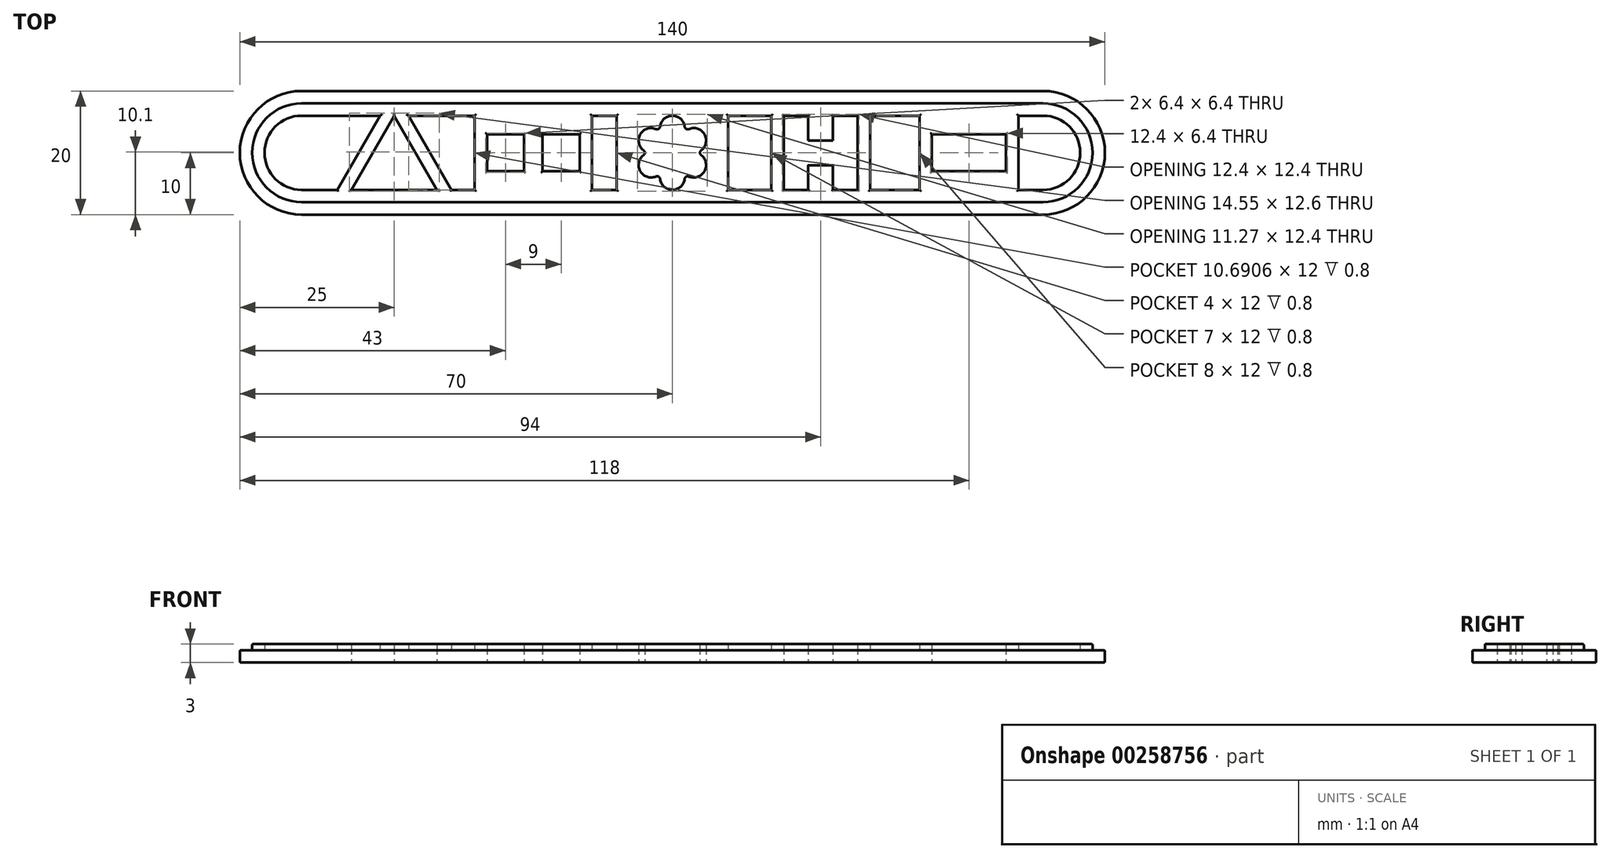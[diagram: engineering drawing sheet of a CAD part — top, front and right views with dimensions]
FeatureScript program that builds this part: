
annotation { "Feature Type Name" : "Feature", "Feature Type Description" : "" }
export const myFeature = defineFeature(function(context is Context, id is Id, definition is map)
    precondition{}
    {
        {
            var Q0;
            Q0=qCreatedBy(makeId("Top.planeOp"),FACE);
            var sketch = newSketch(context, id + "F0", { "sketchPlane" : qUnion([Q0])});
            skLineSegment(sketch, "E0.bottom", {"start": v(-60, -10) * mm, "end": v(60, -10) * mm});
            skLineSegment(sketch, "E0.top", {"start": v(-60, 10) * mm, "end": v(60, 10) * mm});
            skPoint(sketch, "E0.middle", {"position": v(0, 0) * mm});
            skArc(sketch, "E1", {"start": v(-60, 10) * mm, "mid": v(-70, 0) * mm, "end": v(-60, -10) * mm});
            skArc(sketch, "E2", {"start": v(60, -10) * mm, "mid": v(70, 0) * mm, "end": v(60, 10) * mm});
            skLineSegment(sketch, "E3", {"start": v(-70, 0) * mm, "end": v(70, 0) * mm, "construction": true});
            skArc(sketch, "E4", {"start": v(1.99, 4.24) * mm, "mid": v(0, 6) * mm, "end": v(-1.99, 4.24) * mm});
            skArc(sketch, "E5.1.0", {"start": v(-2.68, 3.84) * mm, "mid": v(-5.2, 3) * mm, "end": v(-4.66, 0.4) * mm});
            skArc(sketch, "E5.2.0", {"start": v(-4.66, -0.4) * mm, "mid": v(-5.2, -3) * mm, "end": v(-2.68, -3.84) * mm});
            skArc(sketch, "E5.3.0", {"start": v(-1.99, -4.24) * mm, "mid": v(0, -6) * mm, "end": v(1.99, -4.24) * mm});
            skArc(sketch, "E5.4.0", {"start": v(2.68, -3.84) * mm, "mid": v(5.2, -3) * mm, "end": v(4.66, -0.4) * mm});
            skArc(sketch, "E5.5.0", {"start": v(4.66, 0.4) * mm, "mid": v(5.2, 3) * mm, "end": v(2.68, 3.84) * mm});
            skPoint(sketch, "E6.visualSharp", {"position": v(-1.73, 3) * mm});
            skArc(sketch, "E6.filletArc", {"start": v(-2.68, 3.84) * mm, "mid": v(-2.23, 3.87) * mm, "end": v(-1.99, 4.24) * mm});
            skPoint(sketch, "E7.visualSharp", {"position": v(1.73, 3) * mm});
            skArc(sketch, "E7.filletArc", {"start": v(1.99, 4.24) * mm, "mid": v(2.23, 3.87) * mm, "end": v(2.68, 3.84) * mm});
            skPoint(sketch, "E8.visualSharp", {"position": v(3.46, 0) * mm});
            skArc(sketch, "E8.filletArc", {"start": v(4.66, 0.4) * mm, "mid": v(4.46, 0) * mm, "end": v(4.66, -0.4) * mm});
            skPoint(sketch, "E9.visualSharp", {"position": v(1.73, -3) * mm});
            skArc(sketch, "E9.filletArc", {"start": v(2.68, -3.84) * mm, "mid": v(2.23, -3.87) * mm, "end": v(1.99, -4.24) * mm});
            skPoint(sketch, "E10.visualSharp", {"position": v(-1.73, -3) * mm});
            skArc(sketch, "E10.filletArc", {"start": v(-1.99, -4.24) * mm, "mid": v(-2.23, -3.87) * mm, "end": v(-2.68, -3.84) * mm});
            skPoint(sketch, "E11.visualSharp", {"position": v(-3.46, 0) * mm});
            skArc(sketch, "E11.filletArc", {"start": v(-4.66, -0.4) * mm, "mid": v(-4.46, 0) * mm, "end": v(-4.66, 0.4) * mm});
            skLineSegment(sketch, "E12.bottom", {"start": v(-15, 3) * mm, "end": v(-21, 3) * mm});
            skLineSegment(sketch, "E12.top", {"start": v(-15, -3) * mm, "end": v(-21, -3) * mm});
            skLineSegment(sketch, "E12.left", {"start": v(-15, 3) * mm, "end": v(-15, -3) * mm});
            skLineSegment(sketch, "E12.right", {"start": v(-21, 3) * mm, "end": v(-21, -3) * mm});
            skPoint(sketch, "E12.middle", {"position": v(-18, 0) * mm});
            skLineSegment(sketch, "E13.bottom", {"start": v(-24, -3) * mm, "end": v(-30, -3) * mm});
            skLineSegment(sketch, "E13.top", {"start": v(-24, 3) * mm, "end": v(-30, 3) * mm});
            skLineSegment(sketch, "E13.left", {"start": v(-24, -3) * mm, "end": v(-24, 3) * mm});
            skLineSegment(sketch, "E13.right", {"start": v(-30, -3) * mm, "end": v(-30, 3) * mm});
            skPoint(sketch, "E13.middle", {"position": v(-27, 0) * mm});
            skLineSegment(sketch, "E14", {"start": v(-51.93, -6) * mm, "end": v(-38.07, -6) * mm});
            skLineSegment(sketch, "E15", {"start": v(-38.07, -6) * mm, "end": v(-45, 6) * mm});
            skLineSegment(sketch, "E16", {"start": v(-45, 6) * mm, "end": v(-51.93, -6) * mm});
            skLineSegment(sketch, "E17", {"start": v(-45, 6) * mm, "end": v(-45, -6) * mm, "construction": true});
            skPoint(sketch, "E18", {"position": v(-45, 0) * mm});
            skLineSegment(sketch, "E19", {"start": v(18, 6) * mm, "end": v(18, -6) * mm});
            skLineSegment(sketch, "E20", {"start": v(18, -6) * mm, "end": v(22, -6) * mm});
            skLineSegment(sketch, "E21", {"start": v(22, -6) * mm, "end": v(22, -2) * mm});
            skLineSegment(sketch, "E22", {"start": v(22, -2) * mm, "end": v(26, -2) * mm});
            skLineSegment(sketch, "E23", {"start": v(26, -2) * mm, "end": v(26, -6) * mm});
            skLineSegment(sketch, "E24", {"start": v(26, -6) * mm, "end": v(30, -6) * mm});
            skLineSegment(sketch, "E25", {"start": v(30, -6) * mm, "end": v(30, 6) * mm});
            skLineSegment(sketch, "E26", {"start": v(30, 6) * mm, "end": v(26, 6) * mm});
            skLineSegment(sketch, "E27", {"start": v(26, 6) * mm, "end": v(26, 2) * mm});
            skLineSegment(sketch, "E28", {"start": v(26, 2) * mm, "end": v(22, 2) * mm});
            skLineSegment(sketch, "E29", {"start": v(22, 2) * mm, "end": v(22, 6) * mm});
            skLineSegment(sketch, "E30", {"start": v(22, 6) * mm, "end": v(18, 6) * mm});
            skLineSegment(sketch, "E31", {"start": v(24, 2) * mm, "end": v(24, -2) * mm, "construction": true});
            skPoint(sketch, "E32", {"position": v(24, 0) * mm});
            skLineSegment(sketch, "E33.bottom", {"start": v(54, -3) * mm, "end": v(42, -3) * mm});
            skLineSegment(sketch, "E33.top", {"start": v(54, 3) * mm, "end": v(42, 3) * mm});
            skLineSegment(sketch, "E33.left", {"start": v(54, -3) * mm, "end": v(54, 3) * mm});
            skLineSegment(sketch, "E33.right", {"start": v(42, -3) * mm, "end": v(42, 3) * mm});
            skPoint(sketch, "E33.middle", {"position": v(48, 0) * mm});
            skSolve(sketch);
        }
        {
            var Q0;
            Q0=makeQuery(id+"F0.imprint","IMPRINT",FACE,{"disambiguationData":[TD([[makeQuery(id+"F0.imprint","IMPRINT",EDGE,{"derivedFrom":sQuery(id+"F0.wireOp",EDGE,"E0.bottom")}),1.0]])]});
            extrude(context, id + "F1", {"entities" : qUnion([Q0]), "depth" : 2 * mm});
        }
        {
            var Q0;
            Q0=makeQuery(id+"F1.opExtrude","CAP_FACE",FACE,{"disambiguationData":[OSD([sQuery(id+"F0.wireOp",EDGE,"E0.bottom"),sQuery(id+"F0.wireOp",EDGE,"E0.top"),sQuery(id+"F0.wireOp",EDGE,"E1"),sQuery(id+"F0.wireOp",EDGE,"E2"),sQuery(id+"F0.wireOp",EDGE,"E4"),sQuery(id+"F0.wireOp",EDGE,"E5.1.0"),sQuery(id+"F0.wireOp",EDGE,"E5.2.0"),sQuery(id+"F0.wireOp",EDGE,"E5.3.0"),sQuery(id+"F0.wireOp",EDGE,"E5.4.0"),sQuery(id+"F0.wireOp",EDGE,"E5.5.0"),sQuery(id+"F0.wireOp",EDGE,"E6.filletArc"),sQuery(id+"F0.wireOp",EDGE,"E7.filletArc"),sQuery(id+"F0.wireOp",EDGE,"E8.filletArc"),sQuery(id+"F0.wireOp",EDGE,"E9.filletArc"),sQuery(id+"F0.wireOp",EDGE,"E10.filletArc"),sQuery(id+"F0.wireOp",EDGE,"E11.filletArc"),sQuery(id+"F0.wireOp",EDGE,"E12.bottom"),sQuery(id+"F0.wireOp",EDGE,"E12.top"),sQuery(id+"F0.wireOp",EDGE,"E12.left"),sQuery(id+"F0.wireOp",EDGE,"E12.right"),sQuery(id+"F0.wireOp",EDGE,"E13.bottom"),sQuery(id+"F0.wireOp",EDGE,"E13.top"),sQuery(id+"F0.wireOp",EDGE,"E13.left"),sQuery(id+"F0.wireOp",EDGE,"E13.right"),sQuery(id+"F0.wireOp",EDGE,"E14"),sQuery(id+"F0.wireOp",EDGE,"E15"),sQuery(id+"F0.wireOp",EDGE,"E16"),sQuery(id+"F0.wireOp",EDGE,"E19"),sQuery(id+"F0.wireOp",EDGE,"E20"),sQuery(id+"F0.wireOp",EDGE,"E21"),sQuery(id+"F0.wireOp",EDGE,"E22"),sQuery(id+"F0.wireOp",EDGE,"E23"),sQuery(id+"F0.wireOp",EDGE,"E24"),sQuery(id+"F0.wireOp",EDGE,"E25"),sQuery(id+"F0.wireOp",EDGE,"E26"),sQuery(id+"F0.wireOp",EDGE,"E27"),sQuery(id+"F0.wireOp",EDGE,"E28"),sQuery(id+"F0.wireOp",EDGE,"E29"),sQuery(id+"F0.wireOp",EDGE,"E30"),sQuery(id+"F0.wireOp",EDGE,"E33.bottom"),sQuery(id+"F0.wireOp",EDGE,"E33.top"),sQuery(id+"F0.wireOp",EDGE,"E33.left"),sQuery(id+"F0.wireOp",EDGE,"E33.right")])],"isStart":false});
            var sketch = newSketch(context, id + "F2", { "sketchPlane" : qUnion([Q0])});
            skLineSegment(sketch, "E34.0", {"start": v(60, 8) * mm, "end": v(54, 8) * mm});
            skArc(sketch, "E34.1", {"start": v(60, -8) * mm, "mid": v(68, 0) * mm, "end": v(60, 8) * mm});
            skArc(sketch, "E34.3", {"start": v(-60, 8) * mm, "mid": v(-68, 0) * mm, "end": v(-60, -8) * mm});
            skLineSegment(sketch, "E35.0.0", {"start": v(-38.07, -6) * mm, "end": v(-45, 6) * mm});
            skLineSegment(sketch, "E35.0.1", {"start": v(-45, 6) * mm, "end": v(-51.93, -6) * mm});
            skLineSegment(sketch, "E35.0.2", {"start": v(-51.93, -6) * mm, "end": v(-38.07, -6) * mm});
            skLineSegment(sketch, "E36.0.0", {"start": v(-24, -3) * mm, "end": v(-24, 3) * mm});
            skLineSegment(sketch, "E36.0.1", {"start": v(-24, 3) * mm, "end": v(-30, 3) * mm});
            skLineSegment(sketch, "E36.0.2", {"start": v(-30, 3) * mm, "end": v(-30, -3) * mm});
            skLineSegment(sketch, "E36.0.3", {"start": v(-30, -3) * mm, "end": v(-24, -3) * mm});
            skLineSegment(sketch, "E37.0.0", {"start": v(-21, -3) * mm, "end": v(-15, -3) * mm});
            skLineSegment(sketch, "E37.0.1", {"start": v(-15, -3) * mm, "end": v(-15, 3) * mm});
            skLineSegment(sketch, "E37.0.2", {"start": v(-15, 3) * mm, "end": v(-21, 3) * mm});
            skLineSegment(sketch, "E37.0.3", {"start": v(-21, 3) * mm, "end": v(-21, -3) * mm});
            skArc(sketch, "E38.0.0", {"start": v(-2.68, -3.84) * mm, "mid": v(-2.23, -3.87) * mm, "end": v(-1.99, -4.24) * mm});
            skArc(sketch, "E38.0.1", {"start": v(-1.99, -4.24) * mm, "mid": v(0, -6) * mm, "end": v(1.99, -4.24) * mm});
            skArc(sketch, "E38.0.2", {"start": v(1.99, -4.24) * mm, "mid": v(2.23, -3.87) * mm, "end": v(2.68, -3.84) * mm});
            skArc(sketch, "E38.0.3", {"start": v(2.68, -3.84) * mm, "mid": v(5.2, -3) * mm, "end": v(4.66, -0.4) * mm});
            skArc(sketch, "E38.0.4", {"start": v(4.66, -0.4) * mm, "mid": v(4.46, 0) * mm, "end": v(4.66, 0.4) * mm});
            skArc(sketch, "E38.0.5", {"start": v(4.66, 0.4) * mm, "mid": v(5.2, 3) * mm, "end": v(2.68, 3.84) * mm});
            skArc(sketch, "E38.0.6", {"start": v(2.68, 3.84) * mm, "mid": v(2.23, 3.87) * mm, "end": v(1.99, 4.24) * mm});
            skArc(sketch, "E38.0.7", {"start": v(1.99, 4.24) * mm, "mid": v(0, 6) * mm, "end": v(-1.99, 4.24) * mm});
            skArc(sketch, "E38.0.8", {"start": v(-1.99, 4.24) * mm, "mid": v(-2.23, 3.87) * mm, "end": v(-2.68, 3.84) * mm});
            skArc(sketch, "E38.0.9", {"start": v(-2.68, 3.84) * mm, "mid": v(-5.2, 3) * mm, "end": v(-4.66, 0.4) * mm});
            skArc(sketch, "E38.0.10", {"start": v(-4.66, 0.4) * mm, "mid": v(-4.46, 0) * mm, "end": v(-4.66, -0.4) * mm});
            skArc(sketch, "E38.0.11", {"start": v(-4.66, -0.4) * mm, "mid": v(-5.2, -3) * mm, "end": v(-2.68, -3.84) * mm});
            skLineSegment(sketch, "E39.0.0", {"start": v(22, 2) * mm, "end": v(22, 6) * mm});
            skLineSegment(sketch, "E39.0.1", {"start": v(22, 6) * mm, "end": v(18, 6) * mm});
            skLineSegment(sketch, "E39.0.2", {"start": v(18, 6) * mm, "end": v(18, -6) * mm});
            skLineSegment(sketch, "E39.0.3", {"start": v(18, -6) * mm, "end": v(22, -6) * mm});
            skLineSegment(sketch, "E39.0.4", {"start": v(22, -6) * mm, "end": v(22, -2) * mm});
            skLineSegment(sketch, "E39.0.5", {"start": v(22, -2) * mm, "end": v(26, -2) * mm});
            skLineSegment(sketch, "E39.0.6", {"start": v(26, -2) * mm, "end": v(26, -6) * mm});
            skLineSegment(sketch, "E39.0.7", {"start": v(26, -6) * mm, "end": v(30, -6) * mm});
            skLineSegment(sketch, "E39.0.8", {"start": v(30, -6) * mm, "end": v(30, 6) * mm});
            skLineSegment(sketch, "E39.0.9", {"start": v(30, 6) * mm, "end": v(26, 6) * mm});
            skLineSegment(sketch, "E39.0.10", {"start": v(26, 6) * mm, "end": v(26, 2) * mm});
            skLineSegment(sketch, "E39.0.11", {"start": v(26, 2) * mm, "end": v(22, 2) * mm});
            skLineSegment(sketch, "E40.0.0", {"start": v(54, -3) * mm, "end": v(54, 3) * mm});
            skLineSegment(sketch, "E40.0.1", {"start": v(54, 3) * mm, "end": v(42, 3) * mm});
            skLineSegment(sketch, "E40.0.2", {"start": v(42, 3) * mm, "end": v(42, -3) * mm});
            skLineSegment(sketch, "E40.0.3", {"start": v(42, -3) * mm, "end": v(54, -3) * mm});
            skLineSegment(sketch, "E41.0.0", {"start": v(60, 10) * mm, "end": v(-60, 10) * mm});
            skArc(sketch, "E41.0.1", {"start": v(-60, 10) * mm, "mid": v(-70, 0) * mm, "end": v(-60, -10) * mm});
            skLineSegment(sketch, "E41.0.2", {"start": v(-60, -10) * mm, "end": v(60, -10) * mm});
            skArc(sketch, "E41.0.3", {"start": v(60, -10) * mm, "mid": v(70, 0) * mm, "end": v(60, 10) * mm});
            skLineSegment(sketch, "E42", {"start": v(-30, 8) * mm, "end": v(-30, -8) * mm});
            skLineSegment(sketch, "E43", {"start": v(-15, 8) * mm, "end": v(-15, -8) * mm});
            skLineSegment(sketch, "E44", {"start": v(7, 8) * mm, "end": v(7, -8) * mm});
            skLineSegment(sketch, "E45", {"start": v(-7, 8) * mm, "end": v(-7, -8) * mm});
            skLineSegment(sketch, "E46", {"start": v(18, 8) * mm, "end": v(18, -8) * mm});
            skLineSegment(sketch, "E47", {"start": v(30, 8) * mm, "end": v(30, -8) * mm});
            skLineSegment(sketch, "E48", {"start": v(42, 8) * mm, "end": v(42, -8) * mm});
            skLineSegment(sketch, "E49", {"start": v(54, 8) * mm, "end": v(54, -8) * mm});
            skLineSegment(sketch, "E50", {"start": v(-60, -8) * mm, "end": v(-53.08, -8) * mm});
            skLineSegment(sketch, "E51", {"start": v(-30, 8) * mm, "end": v(-43.85, 8) * mm});
            skLineSegment(sketch, "E52", {"start": v(-15, 8) * mm, "end": v(-30, 8) * mm});
            skLineSegment(sketch, "E53", {"start": v(-15, -8) * mm, "end": v(-7, -8) * mm});
            skLineSegment(sketch, "E54", {"start": v(-7, -8) * mm, "end": v(7, -8) * mm});
            skLineSegment(sketch, "E55", {"start": v(7, -8) * mm, "end": v(18, -8) * mm});
            skLineSegment(sketch, "E56", {"start": v(18, -8) * mm, "end": v(30, -8) * mm});
            skLineSegment(sketch, "E57", {"start": v(30, -8) * mm, "end": v(42, -8) * mm});
            skLineSegment(sketch, "E58", {"start": v(42, -8) * mm, "end": v(54, -8) * mm});
            skLineSegment(sketch, "E59", {"start": v(54, -8) * mm, "end": v(60, -8) * mm});
            skLineSegment(sketch, "E60", {"start": v(54, 8) * mm, "end": v(42, 8) * mm});
            skLineSegment(sketch, "E61", {"start": v(42, 8) * mm, "end": v(30, 8) * mm});
            skLineSegment(sketch, "E62", {"start": v(30, 8) * mm, "end": v(18, 8) * mm});
            skLineSegment(sketch, "E63", {"start": v(18, 8) * mm, "end": v(7, 8) * mm});
            skLineSegment(sketch, "E64", {"start": v(7, 8) * mm, "end": v(-7, 8) * mm});
            skLineSegment(sketch, "E65", {"start": v(-7, 8) * mm, "end": v(-15, 8) * mm});
            skLineSegment(sketch, "E66.0", {"start": v(-9, 6) * mm, "end": v(-13, 6) * mm});
            skLineSegment(sketch, "E66.1", {"start": v(-9, 6) * mm, "end": v(-9, -6) * mm});
            skLineSegment(sketch, "E66.2", {"start": v(-13, -6) * mm, "end": v(-9, -6) * mm});
            skLineSegment(sketch, "E66.3", {"start": v(-13, 6) * mm, "end": v(-13, -6) * mm});
            skLineSegment(sketch, "E67.0", {"start": v(16, 6) * mm, "end": v(9, 6) * mm});
            skLineSegment(sketch, "E67.1", {"start": v(16, 6) * mm, "end": v(16, -6) * mm});
            skLineSegment(sketch, "E67.2", {"start": v(9, -6) * mm, "end": v(16, -6) * mm});
            skLineSegment(sketch, "E67.3", {"start": v(9, 6) * mm, "end": v(9, -6) * mm});
            skLineSegment(sketch, "E68.0", {"start": v(40, 6) * mm, "end": v(32, 6) * mm});
            skLineSegment(sketch, "E68.1", {"start": v(40, 6) * mm, "end": v(40, -6) * mm});
            skLineSegment(sketch, "E68.2", {"start": v(32, -6) * mm, "end": v(40, -6) * mm});
            skLineSegment(sketch, "E68.3", {"start": v(32, 6) * mm, "end": v(32, -6) * mm});
            skArc(sketch, "E69.0", {"start": v(60, -6) * mm, "mid": v(66, 0) * mm, "end": v(60, 6) * mm});
            skLineSegment(sketch, "E69.1", {"start": v(56, -6) * mm, "end": v(60, -6) * mm});
            skLineSegment(sketch, "E69.2", {"start": v(56, 6) * mm, "end": v(56, -6) * mm});
            skLineSegment(sketch, "E69.3", {"start": v(60, 6) * mm, "end": v(56, 6) * mm});
            skLineSegment(sketch, "E70", {"start": v(-43.85, 8) * mm, "end": v(-53.08, -8) * mm});
            skLineSegment(sketch, "E71", {"start": v(-46.15, 8) * mm, "end": v(-36.92, -8) * mm});
            skLineSegment(sketch, "E72", {"start": v(-46.15, 8) * mm, "end": v(-60, 8) * mm});
            skLineSegment(sketch, "E73", {"start": v(-43.85, 8) * mm, "end": v(-46.15, 8) * mm});
            skLineSegment(sketch, "E74", {"start": v(-36.92, -8) * mm, "end": v(-30, -8) * mm});
            skLineSegment(sketch, "E75", {"start": v(-53.08, -8) * mm, "end": v(-36.92, -8) * mm});
            skLineSegment(sketch, "E76.0", {"start": v(-47.3, 6) * mm, "end": v(-54.24, -6) * mm});
            skLineSegment(sketch, "E76.1", {"start": v(-47.3, 6) * mm, "end": v(-60, 6) * mm});
            skArc(sketch, "E76.2", {"start": v(-60, 6) * mm, "mid": v(-66, 0) * mm, "end": v(-60, -6) * mm});
            skLineSegment(sketch, "E76.3", {"start": v(-60, -6) * mm, "end": v(-54.24, -6) * mm});
            skLineSegment(sketch, "E77", {"start": v(-30, -8) * mm, "end": v(-15, -8) * mm});
            skLineSegment(sketch, "E78.0", {"start": v(-42.7, 6) * mm, "end": v(-35.76, -6) * mm});
            skLineSegment(sketch, "E78.1", {"start": v(-32, 6) * mm, "end": v(-42.7, 6) * mm});
            skLineSegment(sketch, "E78.2", {"start": v(-32, 6) * mm, "end": v(-32, -6) * mm});
            skLineSegment(sketch, "E78.3", {"start": v(-35.76, -6) * mm, "end": v(-32, -6) * mm});
            skSolve(sketch);
        }
        {
            var Q0;
            Q0=makeQuery(id+"F2.imprint","IMPRINT",FACE,{"disambiguationData":[TD([[makeQuery(id+"F2.imprint","IMPRINT",EDGE,{"derivedFrom":sQuery(id+"F2.wireOp",EDGE,"E34.3")}),1.0]])]});
            var Q1;
            {var subQ0=sQuery(id+"F2.wireOp",EDGE,"E35.0.2");Q1=makeQuery(id+"F2.imprint","IMPRINT",FACE,{"disambiguationData":[TD([[makeQuery(id+"F2.imprint","IMPRINT",EDGE,{"derivedFrom":subQ0}),-1.0]])]});}
            var Q2;
            {var subQ3=sQuery(id+"F2.wireOp",EDGE,"E73");Q2=makeQuery(id+"F2.imprint","IMPRINT",FACE,{"disambiguationData":[TD([[makeQuery(id+"F2.imprint","IMPRINT",EDGE,{"derivedFrom":subQ3}),1.0]])]});}
            var Q3;
            {var subQ5=sQuery(id+"F2.wireOp",EDGE,"E51");Q3=makeQuery(id+"F2.imprint","IMPRINT",FACE,{"disambiguationData":[TD([[makeQuery(id+"F2.imprint","IMPRINT",EDGE,{"derivedFrom":subQ5}),1.0]])]});}
            var Q4;
            Q4=makeQuery(id+"F2.imprint","IMPRINT",FACE,{"disambiguationData":[TD([[makeQuery(id+"F2.imprint","IMPRINT",EDGE,{"derivedFrom":sQuery(id+"F2.wireOp",EDGE,"E45")}),-1.0]])]});
            var Q5;
            Q5=makeQuery(id+"F2.imprint","IMPRINT",FACE,{"disambiguationData":[TD([[makeQuery(id+"F2.imprint","IMPRINT",EDGE,{"derivedFrom":sQuery(id+"F2.wireOp",EDGE,"E36.0.0")}),-1.0]])]});
            var Q6;
            Q6=makeQuery(id+"F2.imprint","IMPRINT",FACE,{"disambiguationData":[TD([[makeQuery(id+"F2.imprint","IMPRINT",EDGE,{"derivedFrom":sQuery(id+"F2.wireOp",EDGE,"E38.0.0")}),1.0]])]});
            var Q7;
            Q7=makeQuery(id+"F2.imprint","IMPRINT",FACE,{"disambiguationData":[TD([[makeQuery(id+"F2.imprint","IMPRINT",EDGE,{"derivedFrom":sQuery(id+"F2.wireOp",EDGE,"E44")}),1.0]])]});
            var Q8;
            Q8=makeQuery(id+"F2.imprint","IMPRINT",FACE,{"disambiguationData":[TD([[makeQuery(id+"F2.imprint","IMPRINT",EDGE,{"derivedFrom":sQuery(id+"F2.wireOp",EDGE,"E39.0.0")}),-1.0]])]});
            var Q9;
            {var subQ0=sQuery(id+"F2.wireOp",EDGE,"E39.0.3");Q9=makeQuery(id+"F2.imprint","IMPRINT",FACE,{"disambiguationData":[TD([[makeQuery(id+"F2.imprint","IMPRINT",EDGE,{"derivedFrom":subQ0}),-1.0]])]});}
            var Q10;
            {var subQ2=sQuery(id+"F2.wireOp",EDGE,"E57");Q10=makeQuery(id+"F2.imprint","IMPRINT",FACE,{"disambiguationData":[TD([[makeQuery(id+"F2.imprint","IMPRINT",EDGE,{"derivedFrom":subQ2}),1.0]])]});}
            var Q11;
            {var subQ0=sQuery(id+"F2.wireOp",EDGE,"E40.0.3");Q11=makeQuery(id+"F2.imprint","IMPRINT",FACE,{"disambiguationData":[TD([[makeQuery(id+"F2.imprint","IMPRINT",EDGE,{"derivedFrom":subQ0}),1.0]])]});}
            var Q12;
            {var subQ0=sQuery(id+"F2.wireOp",EDGE,"E40.0.1");Q12=makeQuery(id+"F2.imprint","IMPRINT",FACE,{"disambiguationData":[TD([[makeQuery(id+"F2.imprint","IMPRINT",EDGE,{"derivedFrom":subQ0}),-1.0]])]});}
            var Q13;
            {var subQ2=sQuery(id+"F2.wireOp",EDGE,"E34.0");Q13=makeQuery(id+"F2.imprint","IMPRINT",FACE,{"disambiguationData":[TD([[makeQuery(id+"F2.imprint","IMPRINT",EDGE,{"derivedFrom":subQ2}),1.0]])]});}
            extrude(context, id + "F3", {"entities" : qUnion([Q0, Q1, Q2, Q3, Q4, Q5, Q6, Q7, Q8, Q9, Q10, Q11, Q12, Q13]), "operationType" : NewBodyOperationType.ADD, "depth" : 1 * mm});
        }
        {
            var Q0;
            Q0=makeQuery(id+"F3.opExtrude","CAP_FACE",FACE,{"disambiguationData":[OSD([sQuery(id+"F2.wireOp",EDGE,"E34.0"),sQuery(id+"F2.wireOp",EDGE,"E34.1"),sQuery(id+"F2.wireOp",EDGE,"E34.3"),sQuery(id+"F2.wireOp",EDGE,"E35.0.2"),sQuery(id+"F2.wireOp",EDGE,"E36.0.0"),sQuery(id+"F2.wireOp",EDGE,"E36.0.1"),sQuery(id+"F2.wireOp",EDGE,"E36.0.3"),sQuery(id+"F2.wireOp",EDGE,"E37.0.0"),sQuery(id+"F2.wireOp",EDGE,"E37.0.2"),sQuery(id+"F2.wireOp",EDGE,"E37.0.3"),sQuery(id+"F2.wireOp",EDGE,"E38.0.0"),sQuery(id+"F2.wireOp",EDGE,"E38.0.1"),sQuery(id+"F2.wireOp",EDGE,"E38.0.2"),sQuery(id+"F2.wireOp",EDGE,"E38.0.3"),sQuery(id+"F2.wireOp",EDGE,"E38.0.4"),sQuery(id+"F2.wireOp",EDGE,"E38.0.5"),sQuery(id+"F2.wireOp",EDGE,"E38.0.6"),sQuery(id+"F2.wireOp",EDGE,"E38.0.7"),sQuery(id+"F2.wireOp",EDGE,"E38.0.8"),sQuery(id+"F2.wireOp",EDGE,"E38.0.9"),sQuery(id+"F2.wireOp",EDGE,"E38.0.10"),sQuery(id+"F2.wireOp",EDGE,"E38.0.11"),sQuery(id+"F2.wireOp",EDGE,"E39.0.0"),sQuery(id+"F2.wireOp",EDGE,"E39.0.1"),sQuery(id+"F2.wireOp",EDGE,"E39.0.3"),sQuery(id+"F2.wireOp",EDGE,"E39.0.4"),sQuery(id+"F2.wireOp",EDGE,"E39.0.5"),sQuery(id+"F2.wireOp",EDGE,"E39.0.6"),sQuery(id+"F2.wireOp",EDGE,"E39.0.7"),sQuery(id+"F2.wireOp",EDGE,"E39.0.9"),sQuery(id+"F2.wireOp",EDGE,"E39.0.10"),sQuery(id+"F2.wireOp",EDGE,"E39.0.11"),sQuery(id+"F2.wireOp",EDGE,"E40.0.1"),sQuery(id+"F2.wireOp",EDGE,"E40.0.3"),sQuery(id+"F2.wireOp",EDGE,"E42"),sQuery(id+"F2.wireOp",EDGE,"E43"),sQuery(id+"F2.wireOp",EDGE,"E46"),sQuery(id+"F2.wireOp",EDGE,"E47"),sQuery(id+"F2.wireOp",EDGE,"E48"),sQuery(id+"F2.wireOp",EDGE,"E49"),sQuery(id+"F2.wireOp",EDGE,"E50"),sQuery(id+"F2.wireOp",EDGE,"E51"),sQuery(id+"F2.wireOp",EDGE,"E52"),sQuery(id+"F2.wireOp",EDGE,"E53"),sQuery(id+"F2.wireOp",EDGE,"E54"),sQuery(id+"F2.wireOp",EDGE,"E55"),sQuery(id+"F2.wireOp",EDGE,"E56"),sQuery(id+"F2.wireOp",EDGE,"E57"),sQuery(id+"F2.wireOp",EDGE,"E58"),sQuery(id+"F2.wireOp",EDGE,"E59"),sQuery(id+"F2.wireOp",EDGE,"E60"),sQuery(id+"F2.wireOp",EDGE,"E61"),sQuery(id+"F2.wireOp",EDGE,"E62"),sQuery(id+"F2.wireOp",EDGE,"E63"),sQuery(id+"F2.wireOp",EDGE,"E64"),sQuery(id+"F2.wireOp",EDGE,"E65"),sQuery(id+"F2.wireOp",EDGE,"E66.0"),sQuery(id+"F2.wireOp",EDGE,"E66.1"),sQuery(id+"F2.wireOp",EDGE,"E66.2"),sQuery(id+"F2.wireOp",EDGE,"E66.3"),sQuery(id+"F2.wireOp",EDGE,"E67.0"),sQuery(id+"F2.wireOp",EDGE,"E67.1"),sQuery(id+"F2.wireOp",EDGE,"E67.2"),sQuery(id+"F2.wireOp",EDGE,"E67.3"),sQuery(id+"F2.wireOp",EDGE,"E68.0"),sQuery(id+"F2.wireOp",EDGE,"E68.1"),sQuery(id+"F2.wireOp",EDGE,"E68.2"),sQuery(id+"F2.wireOp",EDGE,"E68.3"),sQuery(id+"F2.wireOp",EDGE,"E69.0"),sQuery(id+"F2.wireOp",EDGE,"E69.1"),sQuery(id+"F2.wireOp",EDGE,"E69.2"),sQuery(id+"F2.wireOp",EDGE,"E69.3"),sQuery(id+"F2.wireOp",EDGE,"E70"),sQuery(id+"F2.wireOp",EDGE,"E71"),sQuery(id+"F2.wireOp",EDGE,"E72"),sQuery(id+"F2.wireOp",EDGE,"E73"),sQuery(id+"F2.wireOp",EDGE,"E74"),sQuery(id+"F2.wireOp",EDGE,"E75"),sQuery(id+"F2.wireOp",EDGE,"E76.0"),sQuery(id+"F2.wireOp",EDGE,"E76.1"),sQuery(id+"F2.wireOp",EDGE,"E76.2"),sQuery(id+"F2.wireOp",EDGE,"E76.3"),sQuery(id+"F2.wireOp",EDGE,"E77"),sQuery(id+"F2.wireOp",EDGE,"E78.0"),sQuery(id+"F2.wireOp",EDGE,"E78.1"),sQuery(id+"F2.wireOp",EDGE,"E78.2"),sQuery(id+"F2.wireOp",EDGE,"E78.3")])],"isStart":false});
            var Q1;
            {var subQ0=sQuery(id+"F0.wireOp",EDGE,"E2");var subQ1=sQuery(id+"F0.wireOp",EDGE,"E1");var subQ2=sQuery(id+"F0.wireOp",EDGE,"E0.top");var subQ3=sQuery(id+"F0.wireOp",EDGE,"E0.bottom");Q1=makeQuery(id+"F3.boolean.opBoolean","SPLIT",FACE,{"disambiguationData":[TD([makeQuery(id+"F1.opExtrude","SWEPT_FACE",FACE,{"disambiguationData":[OSD([subQ3])]})])],"derivedFrom":makeQuery(id+"F1.opExtrude","CAP_FACE",FACE,{"disambiguationData":[OSD([subQ3,subQ2,subQ1,subQ0,sQuery(id+"F0.wireOp",EDGE,"E4"),sQuery(id+"F0.wireOp",EDGE,"E5.1.0"),sQuery(id+"F0.wireOp",EDGE,"E5.2.0"),sQuery(id+"F0.wireOp",EDGE,"E5.3.0"),sQuery(id+"F0.wireOp",EDGE,"E5.4.0"),sQuery(id+"F0.wireOp",EDGE,"E5.5.0"),sQuery(id+"F0.wireOp",EDGE,"E6.filletArc"),sQuery(id+"F0.wireOp",EDGE,"E7.filletArc"),sQuery(id+"F0.wireOp",EDGE,"E8.filletArc"),sQuery(id+"F0.wireOp",EDGE,"E9.filletArc"),sQuery(id+"F0.wireOp",EDGE,"E10.filletArc"),sQuery(id+"F0.wireOp",EDGE,"E11.filletArc"),sQuery(id+"F0.wireOp",EDGE,"E12.bottom"),sQuery(id+"F0.wireOp",EDGE,"E12.top"),sQuery(id+"F0.wireOp",EDGE,"E12.left"),sQuery(id+"F0.wireOp",EDGE,"E12.right"),sQuery(id+"F0.wireOp",EDGE,"E13.bottom"),sQuery(id+"F0.wireOp",EDGE,"E13.top"),sQuery(id+"F0.wireOp",EDGE,"E13.left"),sQuery(id+"F0.wireOp",EDGE,"E13.right"),sQuery(id+"F0.wireOp",EDGE,"E14"),sQuery(id+"F0.wireOp",EDGE,"E15"),sQuery(id+"F0.wireOp",EDGE,"E16"),sQuery(id+"F0.wireOp",EDGE,"E19"),sQuery(id+"F0.wireOp",EDGE,"E20"),sQuery(id+"F0.wireOp",EDGE,"E21"),sQuery(id+"F0.wireOp",EDGE,"E22"),sQuery(id+"F0.wireOp",EDGE,"E23"),sQuery(id+"F0.wireOp",EDGE,"E24"),sQuery(id+"F0.wireOp",EDGE,"E25"),sQuery(id+"F0.wireOp",EDGE,"E26"),sQuery(id+"F0.wireOp",EDGE,"E27"),sQuery(id+"F0.wireOp",EDGE,"E28"),sQuery(id+"F0.wireOp",EDGE,"E29"),sQuery(id+"F0.wireOp",EDGE,"E30"),sQuery(id+"F0.wireOp",EDGE,"E33.bottom"),sQuery(id+"F0.wireOp",EDGE,"E33.top"),sQuery(id+"F0.wireOp",EDGE,"E33.left"),sQuery(id+"F0.wireOp",EDGE,"E33.right")])],"isStart":false})});}
            var Q2;
            Q2=makeQuery(id+"F1.opExtrude","CAP_FACE",FACE,{"disambiguationData":[OSD([sQuery(id+"F0.wireOp",EDGE,"E0.bottom"),sQuery(id+"F0.wireOp",EDGE,"E0.top"),sQuery(id+"F0.wireOp",EDGE,"E1"),sQuery(id+"F0.wireOp",EDGE,"E2"),sQuery(id+"F0.wireOp",EDGE,"E4"),sQuery(id+"F0.wireOp",EDGE,"E5.1.0"),sQuery(id+"F0.wireOp",EDGE,"E5.2.0"),sQuery(id+"F0.wireOp",EDGE,"E5.3.0"),sQuery(id+"F0.wireOp",EDGE,"E5.4.0"),sQuery(id+"F0.wireOp",EDGE,"E5.5.0"),sQuery(id+"F0.wireOp",EDGE,"E6.filletArc"),sQuery(id+"F0.wireOp",EDGE,"E7.filletArc"),sQuery(id+"F0.wireOp",EDGE,"E8.filletArc"),sQuery(id+"F0.wireOp",EDGE,"E9.filletArc"),sQuery(id+"F0.wireOp",EDGE,"E10.filletArc"),sQuery(id+"F0.wireOp",EDGE,"E11.filletArc"),sQuery(id+"F0.wireOp",EDGE,"E12.bottom"),sQuery(id+"F0.wireOp",EDGE,"E12.top"),sQuery(id+"F0.wireOp",EDGE,"E12.left"),sQuery(id+"F0.wireOp",EDGE,"E12.right"),sQuery(id+"F0.wireOp",EDGE,"E13.bottom"),sQuery(id+"F0.wireOp",EDGE,"E13.top"),sQuery(id+"F0.wireOp",EDGE,"E13.left"),sQuery(id+"F0.wireOp",EDGE,"E13.right"),sQuery(id+"F0.wireOp",EDGE,"E14"),sQuery(id+"F0.wireOp",EDGE,"E15"),sQuery(id+"F0.wireOp",EDGE,"E16"),sQuery(id+"F0.wireOp",EDGE,"E19"),sQuery(id+"F0.wireOp",EDGE,"E20"),sQuery(id+"F0.wireOp",EDGE,"E21"),sQuery(id+"F0.wireOp",EDGE,"E22"),sQuery(id+"F0.wireOp",EDGE,"E23"),sQuery(id+"F0.wireOp",EDGE,"E24"),sQuery(id+"F0.wireOp",EDGE,"E25"),sQuery(id+"F0.wireOp",EDGE,"E26"),sQuery(id+"F0.wireOp",EDGE,"E27"),sQuery(id+"F0.wireOp",EDGE,"E28"),sQuery(id+"F0.wireOp",EDGE,"E29"),sQuery(id+"F0.wireOp",EDGE,"E30"),sQuery(id+"F0.wireOp",EDGE,"E33.bottom"),sQuery(id+"F0.wireOp",EDGE,"E33.top"),sQuery(id+"F0.wireOp",EDGE,"E33.left"),sQuery(id+"F0.wireOp",EDGE,"E33.right")])],"isStart":true});
            fillet(context, id + "F4", {"entities" : qUnion([Q0, Q1, Q2]), "radius" : 0.2 * mm, "tangentPropagation" : true, "allowEdgeOverflow" : false});
        }
    });
